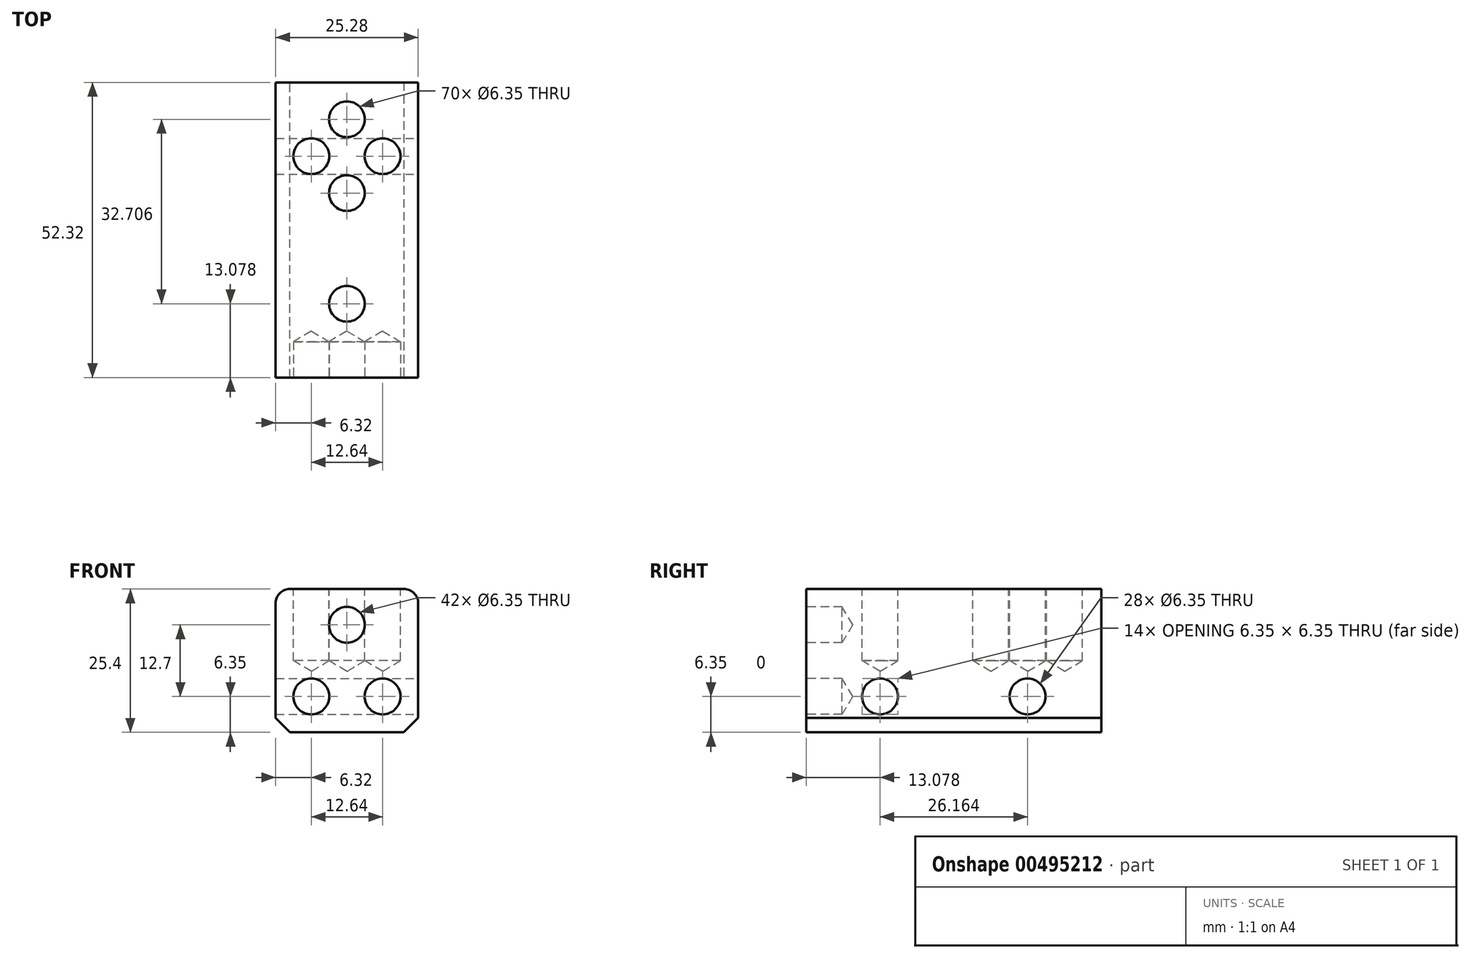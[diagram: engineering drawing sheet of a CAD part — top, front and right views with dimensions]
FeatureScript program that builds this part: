
annotation { "Feature Type Name" : "Feature", "Feature Type Description" : "" }
export const myFeature = defineFeature(function(context is Context, id is Id, definition is map)
    precondition{}
    {
        {
            var Q0;
            Q0=qCreatedBy(makeId("Top.planeOp"),FACE);
            var sketch = newSketch(context, id + "F0", { "sketchPlane" : qUnion([Q0])});
            skLineSegment(sketch, "E0.top", {"start": v(0, -26.16) * mm, "end": v(12.64, -26.16) * mm});
            skLineSegment(sketch, "E0.right", {"start": v(12.64, 0) * mm, "end": v(12.64, -26.16) * mm});
            skLineSegment(sketch, "E1.MirrorCS", {"start": v(-12.64, 0) * mm, "end": v(-12.64, -26.16) * mm});
            skLineSegment(sketch, "E2.MirrorCS", {"start": v(0, -26.16) * mm, "end": v(-12.64, -26.16) * mm});
            skLineSegment(sketch, "E3.MirrorCS", {"start": v(-12.64, 0) * mm, "end": v(-12.64, 26.16) * mm});
            skLineSegment(sketch, "E4.MirrorCS", {"start": v(12.64, 0) * mm, "end": v(12.64, 26.16) * mm});
            skLineSegment(sketch, "E5.MirrorCS", {"start": v(0, 26.16) * mm, "end": v(12.64, 26.16) * mm});
            skLineSegment(sketch, "E6.MirrorCS", {"start": v(0, 26.16) * mm, "end": v(-12.64, 26.16) * mm});
            skSolve(sketch);
        }
        {
            var Q0;
            Q0=makeQuery(id+"F0.imprint","IMPRINT",FACE,{"disambiguationData":[TD([[makeQuery(id+"F0.imprint","IMPRINT",EDGE,{"derivedFrom":sQuery(id+"F0.wireOp",EDGE,"E0.top")}),1.0]])]});
            extrude(context, id + "F1", {"entities" : qUnion([Q0]), "depth" : 25.4 * mm});
        }
        {
            var Q0;
            Q0=makeQuery(id+"F1.opExtrude","SWEPT_FACE",FACE,{"disambiguationData":[OSD([sQuery(id+"F0.wireOp",EDGE,"E0.right"),sQuery(id+"F0.wireOp",EDGE,"E4.MirrorCS")])]});
            var sketch = newSketch(context, id + "F2", { "sketchPlane" : qUnion([Q0])});
            skCircle(sketch, "E7", {"center": v(-13.08, 6.35) * mm, "radius": 3.18 * mm});
            skCircle(sketch, "E8.MirrorC", {"center": v(13.08, 6.35) * mm, "radius": 3.18 * mm});
            skSolve(sketch);
        }
        {
            var Q0;
            Q0=sQuery(id+"F2.wireOp",VERTEX,"E7.center");
            var Q1;
            Q1=sQuery(id+"F2.wireOp",VERTEX,"E8.MirrorC.center");
            var Q2;
            Q2=makeQuery(id+"F1.opExtrude","SWEPT_BODY",BODY,{"disambiguationData":[OSD([sQuery(id+"F0.wireOp",EDGE,"E0.top"),sQuery(id+"F0.wireOp",EDGE,"E0.right"),sQuery(id+"F0.wireOp",EDGE,"E1.MirrorCS"),sQuery(id+"F0.wireOp",EDGE,"E2.MirrorCS"),sQuery(id+"F0.wireOp",EDGE,"E3.MirrorCS"),sQuery(id+"F0.wireOp",EDGE,"E4.MirrorCS"),sQuery(id+"F0.wireOp",EDGE,"E5.MirrorCS"),sQuery(id+"F0.wireOp",EDGE,"E6.MirrorCS")])]});
            hole(context, id + "F3", {"style" : HoleStyle.SIMPLE, "endStyle" : HoleEndStyle.THROUGH, "holeDiameter" : 6.35 * mm, "isTappedThrough" : true, "tappedDepth" : 12.7 * mm, "tapClearance" : 3, "locations" : qUnion([Q0, Q1]), "scope" : qUnion([Q2])});
        }
        {
            var Q0;
            Q0=makeQuery(id+"F1.opExtrude","SWEPT_FACE",FACE,{"disambiguationData":[OSD([sQuery(id+"F0.wireOp",EDGE,"E0.top"),sQuery(id+"F0.wireOp",EDGE,"E2.MirrorCS")])]});
            var sketch = newSketch(context, id + "F4", { "sketchPlane" : qUnion([Q0])});
            skCircle(sketch, "E9", {"center": v(-6.32, 6.35) * mm, "radius": 3.18 * mm});
            skCircle(sketch, "E10.MirrorC", {"center": v(6.32, 6.35) * mm, "radius": 3.18 * mm});
            skCircle(sketch, "E11", {"center": v(0, 19.05) * mm, "radius": 3.18 * mm});
            skLineSegment(sketch, "E12", {"start": v(0, 19.05) * mm, "end": v(6.32, 6.35) * mm});
            skLineSegment(sketch, "E13", {"start": v(6.32, 6.35) * mm, "end": v(-6.32, 6.35) * mm});
            skLineSegment(sketch, "E14", {"start": v(0, 19.05) * mm, "end": v(0, 6.35) * mm});
            skLineSegment(sketch, "E15", {"start": v(0, 6.35) * mm, "end": v(6.32, 6.35) * mm});
            skSolve(sketch);
        }
        {
            var Q0;
            Q0=sQuery(id+"F4.wireOp",VERTEX,"E9.center");
            var Q1;
            Q1=sQuery(id+"F4.wireOp",VERTEX,"E10.MirrorC.center");
            var Q2;
            Q2=sQuery(id+"F4.wireOp",VERTEX,"E11.center");
            var Q3;
            Q3=makeQuery(id+"F1.opExtrude","SWEPT_BODY",BODY,{"disambiguationData":[OSD([sQuery(id+"F0.wireOp",EDGE,"E0.top"),sQuery(id+"F0.wireOp",EDGE,"E0.right"),sQuery(id+"F0.wireOp",EDGE,"E1.MirrorCS"),sQuery(id+"F0.wireOp",EDGE,"E2.MirrorCS"),sQuery(id+"F0.wireOp",EDGE,"E3.MirrorCS"),sQuery(id+"F0.wireOp",EDGE,"E4.MirrorCS"),sQuery(id+"F0.wireOp",EDGE,"E5.MirrorCS"),sQuery(id+"F0.wireOp",EDGE,"E6.MirrorCS")])]});
            hole(context, id + "F5", {"style" : HoleStyle.SIMPLE, "endStyle" : HoleEndStyle.BLIND, "holeDiameter" : 6.35 * mm, "holeDepth" : 6.35 * mm, "isTappedThrough" : true, "tappedDepth" : 12.7 * mm, "tapClearance" : 3, "locations" : qUnion([Q0, Q1, Q2]), "scope" : qUnion([Q3])});
        }
        {
            var Q0;
            Q0=makeQuery(id+"F1.opExtrude","CAP_FACE",FACE,{"disambiguationData":[OSD([sQuery(id+"F0.wireOp",EDGE,"E0.top"),sQuery(id+"F0.wireOp",EDGE,"E0.right"),sQuery(id+"F0.wireOp",EDGE,"E1.MirrorCS"),sQuery(id+"F0.wireOp",EDGE,"E2.MirrorCS"),sQuery(id+"F0.wireOp",EDGE,"E3.MirrorCS"),sQuery(id+"F0.wireOp",EDGE,"E4.MirrorCS"),sQuery(id+"F0.wireOp",EDGE,"E5.MirrorCS"),sQuery(id+"F0.wireOp",EDGE,"E6.MirrorCS")])],"isStart":false});
            var sketch = newSketch(context, id + "F6", { "sketchPlane" : qUnion([Q0])});
            skCircle(sketch, "E16", {"center": v(0, -13.08) * mm, "radius": 6.54 * mm});
            skCircle(sketch, "E17", {"center": v(0, 6.54) * mm, "radius": 3.27 * mm});
            skCircle(sketch, "E18", {"center": v(6.32, 13.08) * mm, "radius": 3.16 * mm});
            skCircle(sketch, "E19.MirrorC", {"center": v(0, 19.62) * mm, "radius": 3.27 * mm});
            skCircle(sketch, "E20.MirrorC", {"center": v(-6.32, 13.08) * mm, "radius": 3.16 * mm});
            skSolve(sketch);
        }
        {
            var Q0;
            Q0=sQuery(id+"F6.wireOp",VERTEX,"E19.MirrorC.center");
            var Q1;
            Q1=sQuery(id+"F6.wireOp",VERTEX,"E17.center");
            var Q2;
            Q2=sQuery(id+"F6.wireOp",VERTEX,"E20.MirrorC.center");
            var Q3;
            Q3=sQuery(id+"F6.wireOp",VERTEX,"E18.center");
            var Q4;
            Q4=sQuery(id+"F6.wireOp",VERTEX,"E16.center");
            var Q5;
            Q5=makeQuery(id+"F1.opExtrude","SWEPT_BODY",BODY,{"disambiguationData":[OSD([sQuery(id+"F0.wireOp",EDGE,"E0.top"),sQuery(id+"F0.wireOp",EDGE,"E0.right"),sQuery(id+"F0.wireOp",EDGE,"E1.MirrorCS"),sQuery(id+"F0.wireOp",EDGE,"E2.MirrorCS"),sQuery(id+"F0.wireOp",EDGE,"E3.MirrorCS"),sQuery(id+"F0.wireOp",EDGE,"E4.MirrorCS"),sQuery(id+"F0.wireOp",EDGE,"E5.MirrorCS"),sQuery(id+"F0.wireOp",EDGE,"E6.MirrorCS")])]});
            hole(context, id + "F7", {"style" : HoleStyle.SIMPLE, "endStyle" : HoleEndStyle.BLIND, "holeDiameter" : 6.35 * mm, "holeDepth" : 12.7 * mm, "isTappedThrough" : true, "tappedDepth" : 12.7 * mm, "tapClearance" : 3, "locations" : qUnion([Q0, Q1, Q2, Q3, Q4]), "scope" : qUnion([Q5])});
        }
        {
            var Q0;
            Q0=makeQuery(id+"F1.opExtrude","CAP_EDGE",EDGE,{"disambiguationData":[OSD([sQuery(id+"F0.wireOp",EDGE,"E0.right"),sQuery(id+"F0.wireOp",EDGE,"E4.MirrorCS")])],"isStart":false});
            var Q1;
            Q1=makeQuery(id+"F1.opExtrude","CAP_EDGE",EDGE,{"disambiguationData":[OSD([sQuery(id+"F0.wireOp",EDGE,"E1.MirrorCS"),sQuery(id+"F0.wireOp",EDGE,"E3.MirrorCS")])],"isStart":false});
            fillet(context, id + "F8", {"entities" : qUnion([Q0, Q1]), "radius" : 2.54 * mm, "tangentPropagation" : true, "allowEdgeOverflow" : false});
        }
        {
            var Q0;
            Q0=makeQuery(id+"F1.opExtrude","CAP_EDGE",EDGE,{"disambiguationData":[OSD([sQuery(id+"F0.wireOp",EDGE,"E1.MirrorCS"),sQuery(id+"F0.wireOp",EDGE,"E3.MirrorCS")])],"isStart":true});
            var Q1;
            Q1=makeQuery(id+"F1.opExtrude","CAP_EDGE",EDGE,{"disambiguationData":[OSD([sQuery(id+"F0.wireOp",EDGE,"E0.right"),sQuery(id+"F0.wireOp",EDGE,"E4.MirrorCS")])],"isStart":true});
            chamfer(context, id + "F9", {"entities" : qUnion([Q0, Q1]), "width" : 2.54 * mm, "tangentPropagation" : true});
        }
    });
